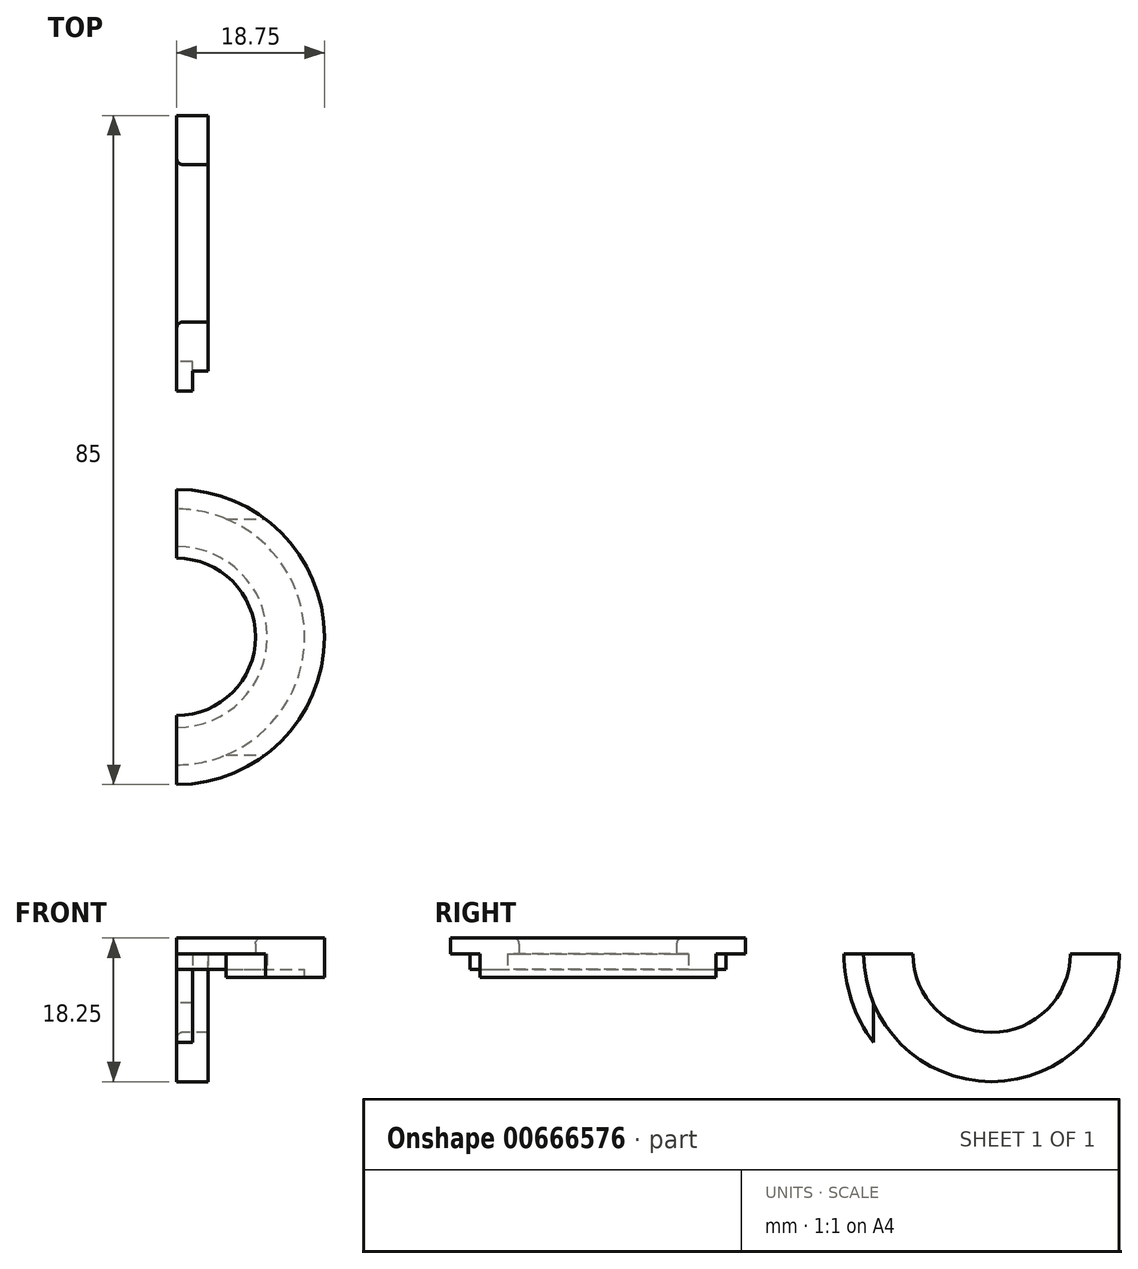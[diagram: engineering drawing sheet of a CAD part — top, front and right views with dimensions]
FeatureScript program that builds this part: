
annotation { "Feature Type Name" : "Feature", "Feature Type Description" : "" }
export const myFeature = defineFeature(function(context is Context, id is Id, definition is map)
    precondition{}
    {
        {
            var Q0;
            Q0=qCreatedBy(makeId("Top.planeOp"),FACE);
            var sketch = newSketch(context, id + "F0", { "sketchPlane" : qUnion([Q0])});
            skCircle(sketch, "E0", {"center": v(0, 0) * mm, "radius": 16.25 * mm});
            skCircle(sketch, "E1", {"center": v(0, 0) * mm, "radius": 18.75 * mm});
            skCircle(sketch, "E2", {"center": v(0, 0) * mm, "radius": 10 * mm});
            skLineSegment(sketch, "E3", {"start": v(0, 0) * mm, "end": v(50, 0) * mm, "construction": true});
            skLineSegment(sketch, "E4", {"start": v(6.25, 15) * mm, "end": v(11.25, 15) * mm});
            skLineSegment(sketch, "E5.MirrorCS", {"start": v(6.25, -15) * mm, "end": v(11.25, -15) * mm});
            skLineSegment(sketch, "E6", {"start": v(0, 0) * mm, "end": v(0, -30) * mm, "construction": true});
            skLineSegment(sketch, "E7", {"start": v(0, -18.75) * mm, "end": v(0, 18.75) * mm});
            skSolve(sketch);
        }
        {
            var Q0;
            {var subQ0=sQuery(id+"F0.wireOp",EDGE,"E4");Q0=makeQuery(id+"F0.imprint","IMPRINT",FACE,{"disambiguationData":[TD([[makeQuery(id+"F0.imprint","IMPRINT",EDGE,{"derivedFrom":subQ0}),1.0]])]});}
            var Q1;
            {var subQ0=sQuery(id+"F0.wireOp",EDGE,"E4");Q1=makeQuery(id+"F0.imprint","IMPRINT",FACE,{"disambiguationData":[TD([[makeQuery(id+"F0.imprint","IMPRINT",EDGE,{"derivedFrom":subQ0}),-1.0]])]});}
            var Q2;
            {var subQ0=sQuery(id+"F0.wireOp",EDGE,"E5.MirrorCS");Q2=makeQuery(id+"F0.imprint","IMPRINT",FACE,{"disambiguationData":[TD([[makeQuery(id+"F0.imprint","IMPRINT",EDGE,{"derivedFrom":subQ0}),-1.0]])]});}
            var Q3;
            {var subQ4=sQuery(id+"F0.wireOp",EDGE,"E0");var subQ5=makeQuery(id+"F0.imprint","INTERSECT",VERTEX,{"derivedFrom":[subQ4,sQuery(id+"F0.wireOp",EDGE,"E4")]});Q3=makeQuery(id+"F0.imprint","IMPRINT",FACE,{"disambiguationData":[TD([[makeQuery(id+"F0.imprint","IMPRINT",EDGE,{"disambiguationData":[TD([[subQ5,-1.0]])],"derivedFrom":subQ4}),1.0]])]});}
            extrude(context, id + "F1", {"entities" : qUnion([Q0, Q1, Q2, Q3]), "depth" : 2 * mm, "offsetDistance" : 25 * mm});
        }
        {
            var Q0;
            {var subQ0=sQuery(id+"F0.wireOp",EDGE,"E4");Q0=makeQuery(id+"F0.imprint","IMPRINT",FACE,{"disambiguationData":[TD([[makeQuery(id+"F0.imprint","IMPRINT",EDGE,{"derivedFrom":subQ0}),-1.0]])]});}
            extrude(context, id + "F2", {"entities" : qUnion([Q0]), "operationType" : NewBodyOperationType.ADD, "oppositeDirection" : true, "depth" : 3 * mm, "offsetDistance" : 25 * mm});
        }
        {
            var Q0;
            {var subQ4=sQuery(id+"F0.wireOp",EDGE,"E0");var subQ5=makeQuery(id+"F0.imprint","INTERSECT",VERTEX,{"derivedFrom":[subQ4,sQuery(id+"F0.wireOp",EDGE,"E4")]});Q0=makeQuery(id+"F0.imprint","IMPRINT",FACE,{"disambiguationData":[TD([[makeQuery(id+"F0.imprint","IMPRINT",EDGE,{"disambiguationData":[TD([[subQ5,-1.0]])],"derivedFrom":subQ4}),1.0]])]});}
            extrude(context, id + "F3", {"entities" : qUnion([Q0]), "operationType" : NewBodyOperationType.ADD, "oppositeDirection" : true, "depth" : 2 * mm, "offsetDistance" : 25 * mm});
        }
        {
            var Q0;
            Q0=qCreatedBy(makeId("Right.planeOp"),FACE);
            var sketch = newSketch(context, id + "F4", { "sketchPlane" : qUnion([Q0])});
            skLineSegment(sketch, "E8", {"start": v(0, 0) * mm, "end": v(100, 0) * mm, "construction": true});
            skLineSegment(sketch, "E9", {"start": v(50, 50) * mm, "end": v(50, -50) * mm, "construction": true});
            skCircle(sketch, "E10", {"center": v(50, 0) * mm, "radius": 18.75 * mm});
            skCircle(sketch, "E11", {"center": v(50, 0) * mm, "radius": 16.25 * mm});
            skCircle(sketch, "E12", {"center": v(50, 0) * mm, "radius": 10 * mm});
            skLineSegment(sketch, "E13", {"start": v(65, -6.25) * mm, "end": v(65, -11.25) * mm});
            skLineSegment(sketch, "E14.MirrorCS", {"start": v(35, -6.25) * mm, "end": v(35, -11.25) * mm});
            skLineSegment(sketch, "E15", {"start": v(68.75, 0) * mm, "end": v(31.25, 0) * mm});
            skSolve(sketch);
        }
        {
            var Q0;
            {var subQ0=sQuery(id+"F4.wireOp",EDGE,"E15");var subQ1=sQuery(id+"F4.wireOp",EDGE,"E11");var subQ2=makeQuery(id+"F4.imprint","INTERSECT",VERTEX,{"disambiguationData":[OD(0.0)],"derivedFrom":[subQ1,subQ0]});Q0=makeQuery(id+"F4.imprint","IMPRINT",FACE,{"disambiguationData":[TD([[makeQuery(id+"F4.imprint","IMPRINT",EDGE,{"disambiguationData":[TD([[subQ2,1.0]])],"derivedFrom":subQ1}),1.0]])]});}
            extrude(context, id + "F5", {"entities" : qUnion([Q0]), "depth" : 4 * mm, "offsetDistance" : 25 * mm});
        }
        {
            var Q0;
            {var subQ0=sQuery(id+"F4.wireOp",EDGE,"E15");var subQ1=sQuery(id+"F4.wireOp",EDGE,"E10");var subQ2=makeQuery(id+"F4.imprint","INTERSECT",VERTEX,{"disambiguationData":[OD(0.0)],"derivedFrom":[subQ1,subQ0]});Q0=makeQuery(id+"F4.imprint","IMPRINT",FACE,{"disambiguationData":[TD([[makeQuery(id+"F4.imprint","IMPRINT",EDGE,{"disambiguationData":[TD([[subQ2,-1.0]])],"derivedFrom":subQ1}),1.0]])]});}
            extrude(context, id + "F6", {"entities" : qUnion([Q0]), "operationType" : NewBodyOperationType.ADD, "depth" : 2 * mm, "offsetDistance" : 25 * mm});
        }
        {
            var Q0;
            Q0=makeQuery(id+"F5.opExtrude","CAP_FACE",FACE,{"disambiguationData":[OSD([sQuery(id+"F4.wireOp",EDGE,"E11"),sQuery(id+"F4.wireOp",EDGE,"E12"),sQuery(id+"F4.wireOp",EDGE,"E15")])],"isStart":false});
            var sketch = newSketch(context, id + "F7", { "sketchPlane" : qUnion([Q0])});
            skArc(sketch, "E16", {"start": v(61.5, 0) * mm, "mid": v(50, 11.5) * mm, "end": v(38.5, 0) * mm});
            skSolve(sketch);
        }
        {
            var Q0;
            {var subQ0=sQuery(id+"F7.wireOp",EDGE,"E16");Q0=makeQuery(id+"F7.imprint","IMPRINT",FACE,{"disambiguationData":[TD([[makeQuery(id+"F7.imprint","IMPRINT",EDGE,{"derivedFrom":subQ0}),1.0]])]});}
            extrude(context, id + "F8", {"entities" : qUnion([Q0]), "operationType" : NewBodyOperationType.REMOVE, "oppositeDirection" : true, "depth" : 2 * mm, "offsetDistance" : 25 * mm});
        }
        {
            var Q0;
            Q0=makeQuery(id+"F5.opExtrude","CAP_EDGE",EDGE,{"disambiguationData":[OSD([sQuery(id+"F4.wireOp",EDGE,"E12")])],"isStart":true});
            var Q1;
            Q1=makeQuery(id+"F8.boolean.opBoolean","COPY",EDGE,{"derivedFrom":makeQuery(id+"F8.opExtrude","CAP_EDGE",EDGE,{"disambiguationData":[OSD([sQuery(id+"F4.wireOp",EDGE,"E12")])],"isStart":false})});
            fillet(context, id + "F9", {"entities" : qUnion([Q0, Q1]), "radius" : 0.75 * mm, "tangentPropagation" : true, "allowEdgeOverflow" : false});
        }
        {
            var Q0;
            Q0=makeQuery(id+"F3.opExtrude","CAP_FACE",FACE,{"disambiguationData":[OSD([sQuery(id+"F0.wireOp",EDGE,"E0"),sQuery(id+"F0.wireOp",EDGE,"E2"),sQuery(id+"F0.wireOp",EDGE,"E7")])],"isStart":false});
            var sketch = newSketch(context, id + "F10", { "sketchPlane" : qUnion([Q0])});
            skLineSegment(sketch, "E17", {"start": v(0, -16.25) * mm, "end": v(0, 16.25) * mm, "construction": true});
            skArc(sketch, "E18", {"start": v(0, -11.5) * mm, "mid": v(11.5, 0) * mm, "end": v(0, 11.5) * mm});
            skSolve(sketch);
        }
        {
            var Q0;
            {var subQ0=sQuery(id+"F10.wireOp",EDGE,"E18");Q0=makeQuery(id+"F10.imprint","IMPRINT",FACE,{"disambiguationData":[TD([[makeQuery(id+"F10.imprint","IMPRINT",EDGE,{"derivedFrom":subQ0}),1.0]])]});}
            extrude(context, id + "F11", {"entities" : qUnion([Q0]), "operationType" : NewBodyOperationType.REMOVE, "oppositeDirection" : true, "depth" : 2 * mm, "offsetDistance" : 25 * mm});
        }
        {
            var Q0;
            Q0=makeQuery(id+"F11.boolean.opBoolean","COPY",EDGE,{"derivedFrom":makeQuery(id+"F11.opExtrude","CAP_EDGE",EDGE,{"disambiguationData":[OSD([sQuery(id+"F0.wireOp",EDGE,"E2")])],"isStart":false})});
            var Q1;
            Q1=makeQuery(id+"F1.opExtrude","CAP_EDGE",EDGE,{"disambiguationData":[OSD([sQuery(id+"F0.wireOp",EDGE,"E2")])],"isStart":false});
            fillet(context, id + "F12", {"entities" : qUnion([Q0, Q1]), "radius" : .75 * mm, "tangentPropagation" : true, "allowEdgeOverflow" : false});
        }
    });
